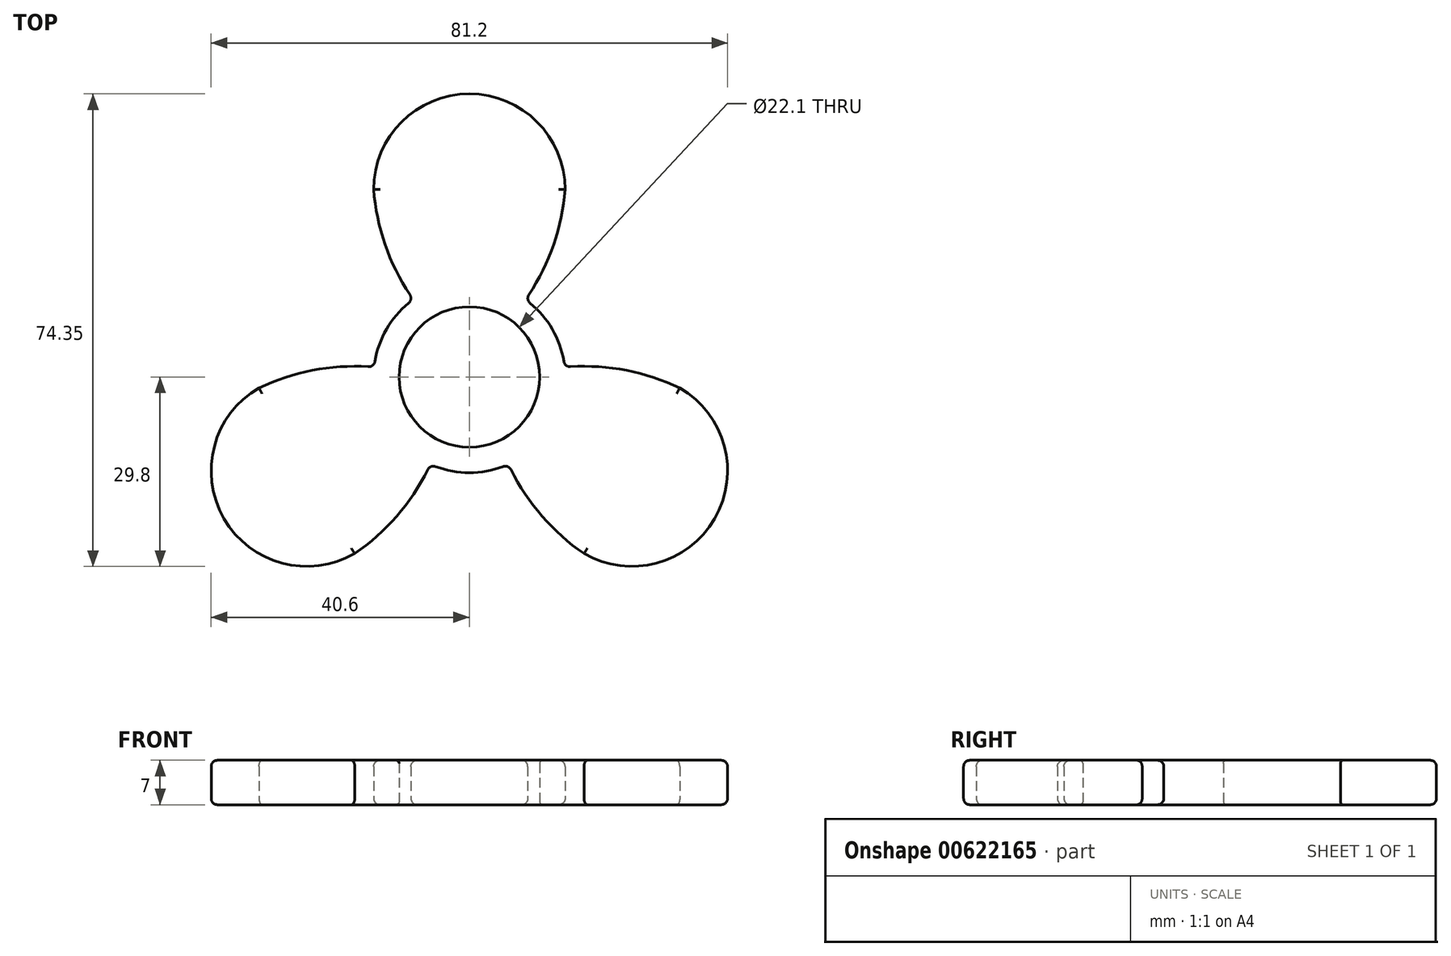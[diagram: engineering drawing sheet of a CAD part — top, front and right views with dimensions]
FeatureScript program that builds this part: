
annotation { "Feature Type Name" : "Feature", "Feature Type Description" : "" }
export const myFeature = defineFeature(function(context is Context, id is Id, definition is map)
    precondition{}
    {
        {
            var Q0;
            Q0=qCreatedBy(makeId("Top.planeOp"),FACE);
            var sketch = newSketch(context, id + "F0", { "sketchPlane" : qUnion([Q0])});
            skCircle(sketch, "E0", {"center": v(0, 0) * mm, "radius": 11.05 * mm});
            skArc(sketch, "E1.0", {"start": v(-9.55, 11.63) * mm, "mid": v(0, -15.05) * mm, "end": v(9.55, 11.63) * mm});
            skLineSegment(sketch, "E2", {"start": v(0, 0) * mm, "end": v(0, 29.5) * mm});
            skCircle(sketch, "E3", {"center": v(0, 29.5) * mm, "radius": 11.05 * mm});
            skArc(sketch, "E4.0", {"start": v(15.05, 29.5) * mm, "mid": v(0, 44.55) * mm, "end": v(-15.05, 29.5) * mm});
            skLineSegment(sketch, "E5", {"start": v(-15.05, 0) * mm, "end": v(15.05, 0) * mm, "construction": true});
            skLineSegment(sketch, "E6", {"start": v(-15.05, 29.5) * mm, "end": v(15.05, 29.5) * mm, "construction": true});
            skArc(sketch, "E7", {"start": v(-15.05, 29.5) * mm, "mid": v(-13.25, 20.87) * mm, "end": v(-9.35, 12.96) * mm});
            skArc(sketch, "E8.MirrorCS", {"start": v(15.05, 29.5) * mm, "mid": v(13.25, 20.87) * mm, "end": v(9.35, 12.96) * mm});
            skPoint(sketch, "E9.trimOffspring.end.orphan", {"position": v(-15.05, 0) * mm});
            skPoint(sketch, "E10.visualSharp", {"position": v(-8.83, 12.19) * mm});
            skArc(sketch, "E10.filletArc", {"start": v(-9.55, 11.63) * mm, "mid": v(-9.2, 12.26) * mm, "end": v(-9.35, 12.96) * mm});
            skPoint(sketch, "E11.visualSharp", {"position": v(8.83, 12.19) * mm});
            skArc(sketch, "E11.filletArc", {"start": v(9.35, 12.96) * mm, "mid": v(9.2, 12.26) * mm, "end": v(9.55, 11.63) * mm});
            skSolve(sketch);
        }
        {
            var Q0;
            Q0=qCreatedBy(makeId("Right.planeOp"),FACE);
            var sketch = newSketch(context, id + "F1", { "sketchPlane" : qUnion([Q0])});
            skLineSegment(sketch, "E12", {"start": v(0, 18.91) * mm, "end": v(0, -18.72) * mm, "construction": true});
            skSolve(sketch);
        }
        {
            var Q0;
            Q0=makeQuery(id+"F0.imprint","IMPRINT",FACE,{"disambiguationData":[TD([[makeQuery(id+"F0.imprint","IMPRINT",EDGE,{"derivedFrom":sQuery(id+"F0.wireOp",EDGE,"E0")}),-1.0]])]});
            var Q1;
            Q1=makeQuery(id+"F0.imprint","IMPRINT",FACE,{"disambiguationData":[TD([[makeQuery(id+"F0.imprint","IMPRINT",EDGE,{"derivedFrom":sQuery(id+"F0.wireOp",EDGE,"E3")}),1.0]])]});
            extrude(context, id + "F2", {"entities" : qUnion([Q0, Q1]), "depth" : 7 * mm, "offsetDistance" : 25 * mm});
        }
        {
            var Q0;
            Q0=makeQuery(id+"F2.opExtrude","SWEPT_BODY",BODY,{"disambiguationData":[OSD([sQuery(id+"F0.wireOp",EDGE,"E0"),sQuery(id+"F0.wireOp",EDGE,"E1.0"),sQuery(id+"F0.wireOp",EDGE,"E3"),sQuery(id+"F0.wireOp",EDGE,"E4.0"),sQuery(id+"F0.wireOp",EDGE,"E7"),sQuery(id+"F0.wireOp",EDGE,"E8.MirrorCS"),sQuery(id+"F0.wireOp",EDGE,"E10.filletArc"),sQuery(id+"F0.wireOp",EDGE,"E11.filletArc")])]});
            var Q1;
            Q1=sQuery(id+"F1.wireOp",EDGE,"E12");
            circularPattern(context, id + "F3", {"operationType" : NewBodyOperationType.ADD, "entities" : qUnion([Q0]), "axis" : qUnion([Q1]), "angle" : 360 * degree, "instanceCount" : 3, "equalSpace" : true});
        }
        {
            var Q0;
            Q0=makeQuery(id+"F3.opPattern","COPY",EDGE,{"derivedFrom":makeQuery(id+"F2.opExtrude","CAP_EDGE",EDGE,{"disambiguationData":[OSD([sQuery(id+"F0.wireOp",EDGE,"E4.0")])],"isStart":false}),"instanceName":"2"});
            var Q1;
            Q1=makeQuery(id+"F3.opPattern","COPY",EDGE,{"derivedFrom":makeQuery(id+"F2.opExtrude","CAP_EDGE",EDGE,{"disambiguationData":[OSD([sQuery(id+"F0.wireOp",EDGE,"E7")])],"isStart":false}),"instanceName":"2"});
            var Q2;
            Q2=makeQuery(id+"F3.opPattern","COPY",EDGE,{"derivedFrom":makeQuery(id+"F2.opExtrude","CAP_EDGE",EDGE,{"disambiguationData":[OSD([sQuery(id+"F0.wireOp",EDGE,"E8.MirrorCS")])],"isStart":false}),"instanceName":"2"});
            var Q3;
            Q3=makeQuery(id+"F3.opPattern","COPY",EDGE,{"derivedFrom":makeQuery(id+"F2.opExtrude","CAP_EDGE",EDGE,{"disambiguationData":[OSD([sQuery(id+"F0.wireOp",EDGE,"E4.0")])],"isStart":false}),"instanceName":"1"});
            var Q4;
            Q4=makeQuery(id+"F3.opPattern","COPY",EDGE,{"derivedFrom":makeQuery(id+"F2.opExtrude","CAP_EDGE",EDGE,{"disambiguationData":[OSD([sQuery(id+"F0.wireOp",EDGE,"E7")])],"isStart":false}),"instanceName":"1"});
            var Q5;
            Q5=makeQuery(id+"F2.opExtrude","CAP_EDGE",EDGE,{"disambiguationData":[OSD([sQuery(id+"F0.wireOp",EDGE,"E4.0")])],"isStart":false});
            var Q6;
            {var subQ0=sQuery(id+"F0.wireOp",EDGE,"E11.filletArc");var subQ2=sQuery(id+"F0.wireOp",EDGE,"E1.0");Q6=makeQuery(id+"F3.boolean.opBoolean","SPLIT",EDGE,{"disambiguationData":[TD([makeQuery(id+"F3.opPattern","COPY",FACE,{"derivedFrom":makeQuery(id+"F2.opExtrude","SWEPT_FACE",FACE,{"disambiguationData":[OSD([subQ0])]}),"instanceName":"1"})])],"derivedFrom":makeQuery(id+"F2.opExtrude","CAP_EDGE",EDGE,{"disambiguationData":[OSD([subQ2])],"isStart":true})});}
            var Q7;
            Q7=makeQuery(id+"F3.opPattern","COPY",EDGE,{"derivedFrom":makeQuery(id+"F2.opExtrude","CAP_EDGE",EDGE,{"disambiguationData":[OSD([sQuery(id+"F0.wireOp",EDGE,"E4.0")])],"isStart":true}),"instanceName":"2"});
            var Q8;
            Q8=makeQuery(id+"F3.opPattern","COPY",EDGE,{"derivedFrom":makeQuery(id+"F2.opExtrude","CAP_EDGE",EDGE,{"disambiguationData":[OSD([sQuery(id+"F0.wireOp",EDGE,"E4.0")])],"isStart":true}),"instanceName":"1"});
            var Q9;
            Q9=makeQuery(id+"F2.opExtrude","CAP_EDGE",EDGE,{"disambiguationData":[OSD([sQuery(id+"F0.wireOp",EDGE,"E4.0")])],"isStart":true});
            var Q10;
            {var subQ1=sQuery(id+"F0.wireOp",EDGE,"E10.filletArc");var subQ2=sQuery(id+"F0.wireOp",EDGE,"E1.0");Q10=makeQuery(id+"F3.boolean.opBoolean","SPLIT",EDGE,{"disambiguationData":[TD([makeQuery(id+"F2.opExtrude","SWEPT_FACE",FACE,{"disambiguationData":[OSD([subQ1])]})])],"derivedFrom":makeQuery(id+"F2.opExtrude","CAP_EDGE",EDGE,{"disambiguationData":[OSD([subQ2])],"isStart":true})});}
            var Q11;
            {var subQ0=sQuery(id+"F0.wireOp",EDGE,"E11.filletArc");var subQ2=sQuery(id+"F0.wireOp",EDGE,"E1.0");Q11=makeQuery(id+"F3.boolean.opBoolean","SPLIT",EDGE,{"disambiguationData":[TD([makeQuery(id+"F2.opExtrude","SWEPT_FACE",FACE,{"disambiguationData":[OSD([subQ0])]})])],"derivedFrom":makeQuery(id+"F2.opExtrude","CAP_EDGE",EDGE,{"disambiguationData":[OSD([subQ2])],"isStart":true})});}
            fillet(context, id + "F4", {"entities" : qUnion([Q0, Q1, Q2, Q3, Q4, Q5, Q6, Q7, Q8, Q9, Q10, Q11]), "radius" : 1 * mm, "tangentPropagation" : true, "allowEdgeOverflow" : false});
        }
        {
            var Q0;
            Q0=makeQuery(id+"F2.opExtrude","CAP_EDGE",EDGE,{"disambiguationData":[OSD([sQuery(id+"F0.wireOp",EDGE,"E0")])],"isStart":true});
            var Q1;
            Q1=makeQuery(id+"F2.opExtrude","CAP_EDGE",EDGE,{"disambiguationData":[OSD([sQuery(id+"F0.wireOp",EDGE,"E0")])],"isStart":false});
            var Q2;
            Q2=makeQuery(id+"F3.opPattern","COPY",EDGE,{"derivedFrom":makeQuery(id+"F2.opExtrude","CAP_EDGE",EDGE,{"disambiguationData":[OSD([sQuery(id+"F0.wireOp",EDGE,"E3")])],"isStart":true}),"instanceName":"1"});
            var Q3;
            Q3=makeQuery(id+"F3.opPattern","COPY",EDGE,{"derivedFrom":makeQuery(id+"F2.opExtrude","CAP_EDGE",EDGE,{"disambiguationData":[OSD([sQuery(id+"F0.wireOp",EDGE,"E3")])],"isStart":false}),"instanceName":"1"});
            var Q4;
            Q4=makeQuery(id+"F2.opExtrude","CAP_EDGE",EDGE,{"disambiguationData":[OSD([sQuery(id+"F0.wireOp",EDGE,"E3")])],"isStart":false});
            var Q5;
            Q5=makeQuery(id+"F2.opExtrude","CAP_EDGE",EDGE,{"disambiguationData":[OSD([sQuery(id+"F0.wireOp",EDGE,"E3")])],"isStart":true});
            var Q6;
            Q6=makeQuery(id+"F3.opPattern","COPY",EDGE,{"derivedFrom":makeQuery(id+"F2.opExtrude","CAP_EDGE",EDGE,{"disambiguationData":[OSD([sQuery(id+"F0.wireOp",EDGE,"E3")])],"isStart":false}),"instanceName":"2"});
            var Q7;
            Q7=makeQuery(id+"F3.opPattern","COPY",EDGE,{"derivedFrom":makeQuery(id+"F2.opExtrude","CAP_EDGE",EDGE,{"disambiguationData":[OSD([sQuery(id+"F0.wireOp",EDGE,"E3")])],"isStart":true}),"instanceName":"2"});
            fillet(context, id + "F5", {"entities" : qUnion([Q0, Q1, Q2, Q3, Q4, Q5, Q6, Q7]), "radius" : 0.5 * mm, "tangentPropagation" : true, "allowEdgeOverflow" : false});
        }
    });
